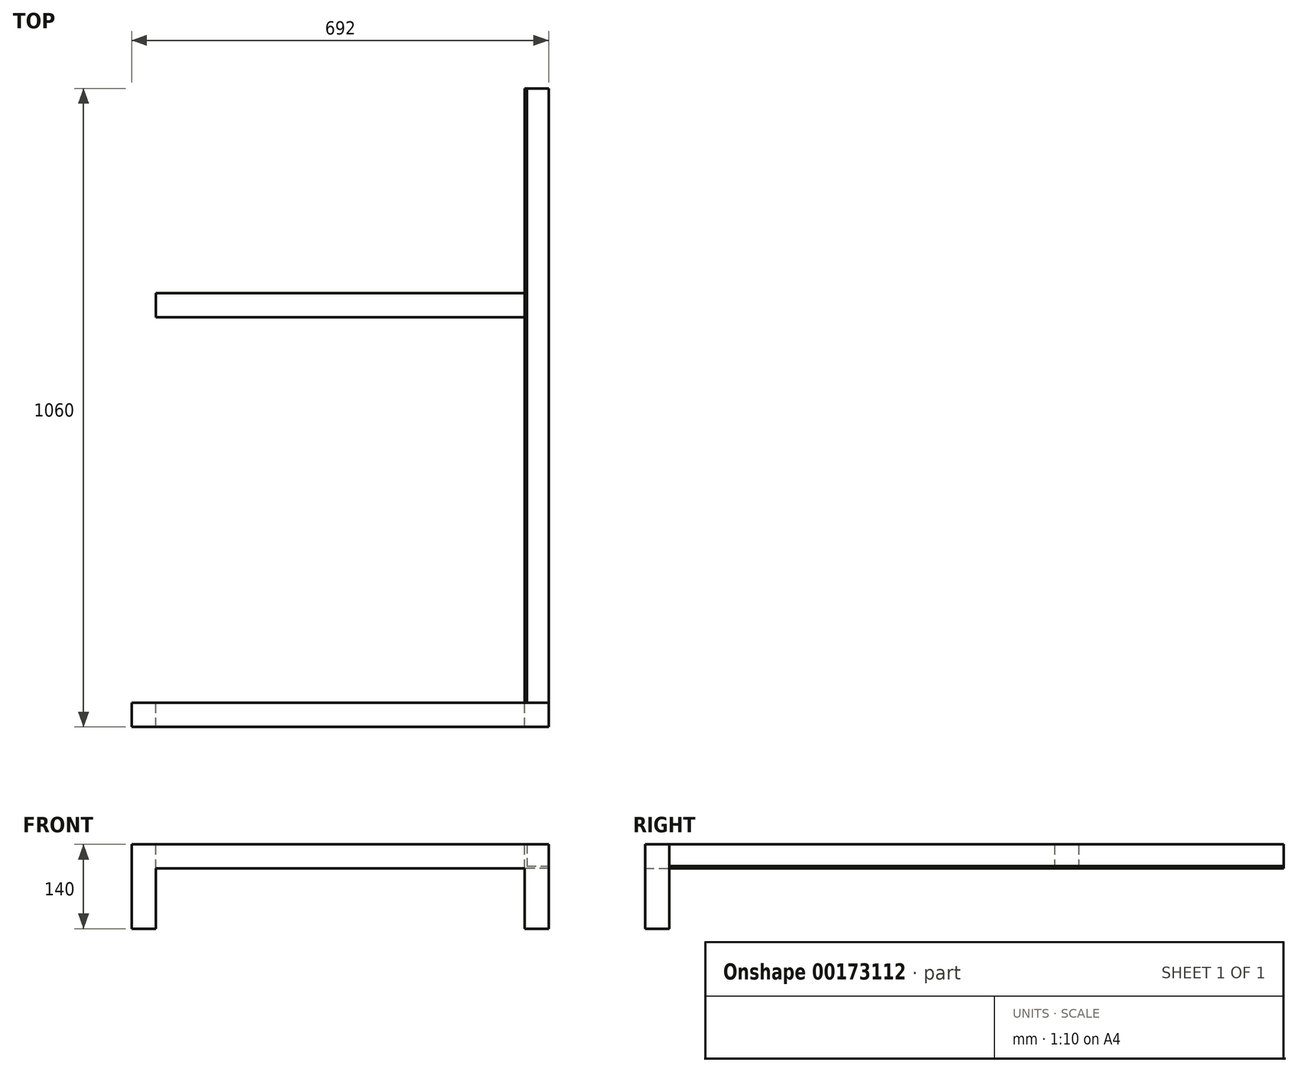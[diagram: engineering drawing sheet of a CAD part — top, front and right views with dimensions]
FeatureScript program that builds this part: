
annotation { "Feature Type Name" : "Feature", "Feature Type Description" : "" }
export const myFeature = defineFeature(function(context is Context, id is Id, definition is map)
    precondition{}
    {
        {
            var Q0;
            Q0=qCreatedBy(makeId("Front.planeOp"),FACE);
            var sketch = newSketch(context, id + "F0", { "sketchPlane" : qUnion([Q0])});
            skLineSegment(sketch, "E0", {"start": v(0, 0) * mm, "end": v(310, 0) * mm, "construction": true});
            skLineSegment(sketch, "E1", {"start": v(0, 0) * mm, "end": v(-310, 0) * mm, "construction": true});
            skLineSegment(sketch, "E2", {"start": v(310, 0) * mm, "end": v(310, -36) * mm});
            skLineSegment(sketch, "E3", {"start": v(310, -36) * mm, "end": v(346, -36) * mm});
            skLineSegment(sketch, "E4", {"start": v(346, -36) * mm, "end": v(346, -40) * mm});
            skLineSegment(sketch, "E5", {"start": v(346, -40) * mm, "end": v(306, -40) * mm});
            skLineSegment(sketch, "E6", {"start": v(306, -40) * mm, "end": v(306, 0) * mm});
            skLineSegment(sketch, "E7", {"start": v(306, 0) * mm, "end": v(310, 0) * mm});
            skSolve(sketch);
        }
        {
            var Q0;
            Q0 = qSketchRegion(id + "F0", true);
            extrude(context, id + "F1", {"entities" : qUnion([Q0]), "endBound" : BoundingType.SYMMETRIC, "depth" : 1020 * mm});
        }
        {
            var Q0;
            Q0=makeQuery(id+"F1.opExtrude","CAP_FACE",FACE,{"disambiguationData":[OSD([sQuery(id+"F0.wireOp",EDGE,"E2"),sQuery(id+"F0.wireOp",EDGE,"E3"),sQuery(id+"F0.wireOp",EDGE,"E4"),sQuery(id+"F0.wireOp",EDGE,"E5"),sQuery(id+"F0.wireOp",EDGE,"E6"),sQuery(id+"F0.wireOp",EDGE,"E7")])],"isStart":false});
            var sketch = newSketch(context, id + "F2", { "sketchPlane" : qUnion([Q0])});
            skLineSegment(sketch, "E8", {"start": v(306, -40) * mm, "end": v(-306, -40) * mm});
            skLineSegment(sketch, "E9", {"start": v(-306, -40) * mm, "end": v(-306, -140) * mm});
            skLineSegment(sketch, "E10", {"start": v(306, -40) * mm, "end": v(306, -140) * mm});
            skLineSegment(sketch, "E11", {"start": v(306, -140) * mm, "end": v(-306, -140) * mm, "construction": true});
            skLineSegment(sketch, "E12.0", {"start": v(346, 0) * mm, "end": v(346, -140) * mm});
            skLineSegment(sketch, "E12.1", {"start": v(346, 0) * mm, "end": v(-346, 0) * mm});
            skLineSegment(sketch, "E12.2", {"start": v(-346, 0) * mm, "end": v(-346, -140) * mm});
            skLineSegment(sketch, "E13", {"start": v(306, -140) * mm, "end": v(346, -140) * mm});
            skLineSegment(sketch, "E14", {"start": v(-346, -140) * mm, "end": v(-306, -140) * mm});
            skSolve(sketch);
        }
        {
            var Q0;
            Q0 = qSketchRegion(id + "F2", true);
            extrude(context, id + "F3", {"entities" : qUnion([Q0]), "depth" : 40 * mm});
        }
        {
            var Q0;
            Q0=makeQuery(id+"F3.opExtrude","SWEPT_FACE",FACE,{"disambiguationData":[OSD([sQuery(id+"F2.wireOp",EDGE,"E12.1")])]});
            var sketch = newSketch(context, id + "F4", { "sketchPlane" : qUnion([Q0])});
            skLineSegment(sketch, "E15.bottom", {"start": v(306, 170) * mm, "end": v(-306, 170) * mm});
            skLineSegment(sketch, "E15.top", {"start": v(306, 130) * mm, "end": v(-306, 130) * mm});
            skLineSegment(sketch, "E15.left", {"start": v(306, 170) * mm, "end": v(306, 130) * mm});
            skLineSegment(sketch, "E15.right", {"start": v(-306, 170) * mm, "end": v(-306, 130) * mm});
            skSolve(sketch);
        }
        {
            var Q0;
            Q0 = qSketchRegion(id + "F4", true);
            extrude(context, id + "F5", {"entities" : qUnion([Q0]), "oppositeDirection" : true, "depth" : 40 * mm});
        }
    });
